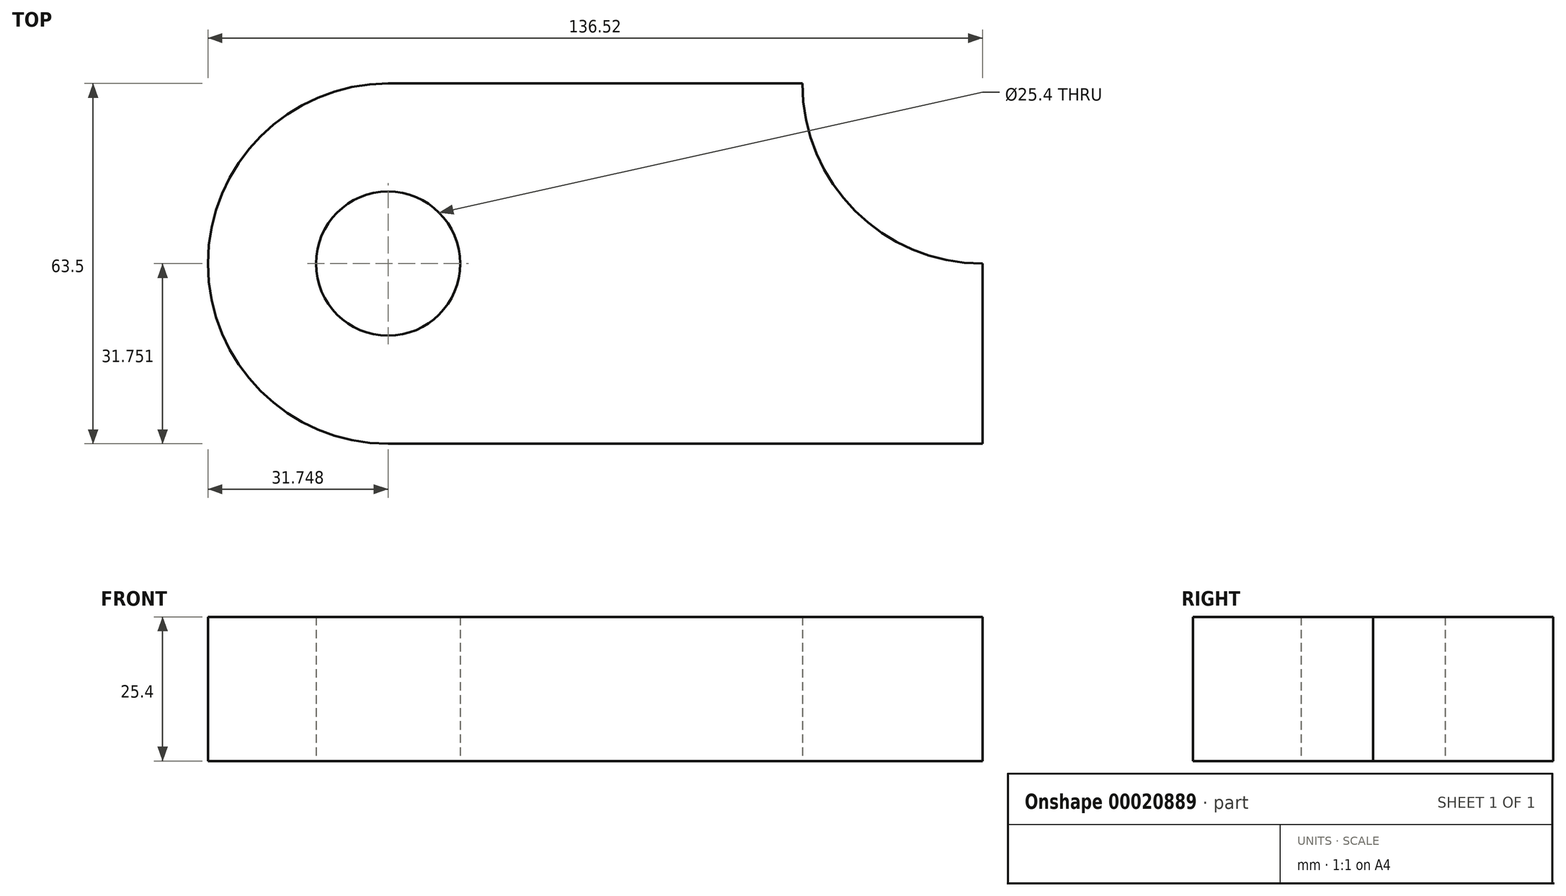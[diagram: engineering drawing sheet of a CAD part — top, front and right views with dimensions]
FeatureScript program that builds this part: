
annotation { "Feature Type Name" : "Feature", "Feature Type Description" : "" }
export const myFeature = defineFeature(function(context is Context, id is Id, definition is map)
    precondition{}
    {
        {
            var Q0;
            Q0=qCreatedBy(makeId("Top.planeOp"),FACE);
            var sketch = newSketch(context, id + "F0", { "sketchPlane" : qUnion([Q0])});
            skLineSegment(sketch, "E0.bottom", {"start": v(-62.05, 34.48) * mm, "end": v(10.97, 34.48) * mm});
            skLineSegment(sketch, "E0.top", {"start": v(-62.05, -29.02) * mm, "end": v(42.72, -29.02) * mm});
            skLineSegment(sketch, "E0.right", {"start": v(42.72, 2.73) * mm, "end": v(42.72, -29.02) * mm});
            skArc(sketch, "E1", {"start": v(-62.05, 34.48) * mm, "mid": v(-93.8, 2.73) * mm, "end": v(-62.05, -29.02) * mm});
            skCircle(sketch, "E2", {"center": v(-62.05, 2.73) * mm, "radius": 12.7 * mm});
            skArc(sketch, "E3", {"start": v(10.97, 34.48) * mm, "mid": v(20.27, 12.03) * mm, "end": v(42.72, 2.73) * mm});
            skSolve(sketch);
        }
        {
            var Q0;
            Q0=makeQuery(id+"F0.imprint","IMPRINT",FACE,{"disambiguationData":[TD([[makeQuery(id+"F0.imprint","IMPRINT",EDGE,{"derivedFrom":sQuery(id+"F0.wireOp",EDGE,"E0.bottom")}),-1.0]])]});
            extrude(context, id + "F1", {"entities" : qUnion([Q0]), "depth" : 25.4 * mm});
        }
    });
